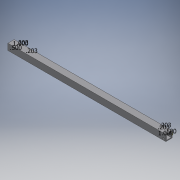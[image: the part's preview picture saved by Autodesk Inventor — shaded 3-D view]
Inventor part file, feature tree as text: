
AUTODESK INVENTOR PART (.ipt)
format: ipt  version: 2018 (Build 220112000, 112)  size: 130,048 bytes
history: native  units: in
note: dims shown in document units (in); Inventor stores cm internally (conversion verified against a paired STEP export)
features: extrude x4, sketch x4
ambient origin geometry x8: Origin, YZ Plane, XZ Plane, XY Plane, X Axis, Y Axis, Z Axis, Center Point
bodies: Solid1 (feature_tree)
feature tree (8):
  extrude  "Extrusion1"  Depth=1.0in
  extrude  "Extrusion5"  Depth=25.0in TaperAngle=0.0deg
  extrude  "Extrusion6"  Depth=24.618in
  extrude  "Extrusion7"  Depth=1.0in TaperAngle=0.0deg
  sketch  "Sketch1"  dims[d0=1.0in d1=1.0in]
  sketch  "Sketch4"  dims[d2=0.125in d3=25.0in d4=0.0in]
  sketch  "Sketch5"  dims[d19=0.256in d20=24.618in]
  sketch  "Sketch7"  dims[d21=0.26in d24=1.0in d25=0.0in d26=3.0in d27=0.5in d28=1.0in d29=0.2031in d30=0.2031in d31=1.0in d32=0.0in d34=0.26in d35=1.0in d36=0.0in]
